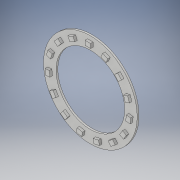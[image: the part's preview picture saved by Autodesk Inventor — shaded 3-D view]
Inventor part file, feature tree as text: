
AUTODESK INVENTOR PART (.ipt)
format: ipt  version: 2019.2 (Build 232265000, 265)  size: 200,192 bytes
history: native  units: mm
features: extrude x2, sketch x2
ambient origin geometry x8: Origin, YZ Plane, XZ Plane, XY Plane, X Axis, Y Axis, Z Axis, Center Point
bodies: Solid1 (feature_tree)
feature tree (4):
  extrude  "Extrusion1"  Depth=44.0mm
  extrude  "Extrusion2"  Depth=1.6mm
  sketch  "Sketch1"  dims[d0=60.0mm d1=44.0mm]
  sketch  "Sketch2"  dims[d2=1.17mm d3=0.0mm d4=52.0mm d5=3.6mm d6=2.8mm d7=150.0mm d9=360.0deg d11=1.6mm d12=0.0mm]
